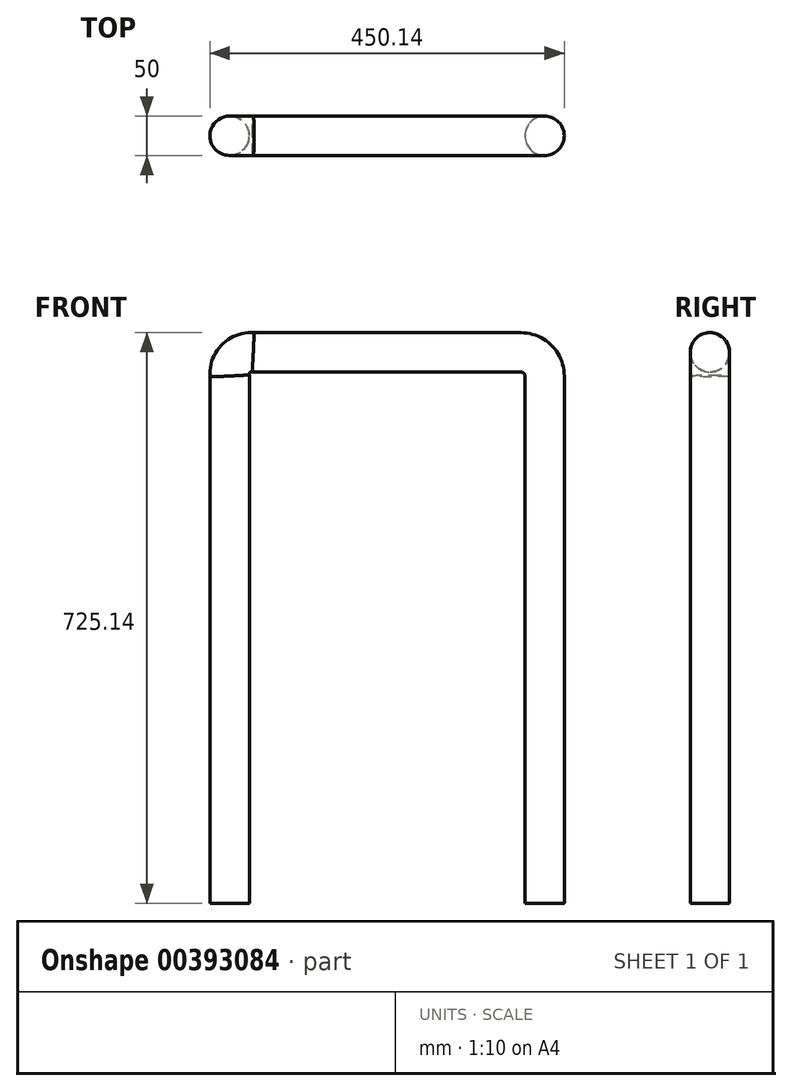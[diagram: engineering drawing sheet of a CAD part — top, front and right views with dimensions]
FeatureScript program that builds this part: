
annotation { "Feature Type Name" : "Feature", "Feature Type Description" : "" }
export const myFeature = defineFeature(function(context is Context, id is Id, definition is map)
    precondition{}
    {
        {
            var Q0;
            Q0=qCreatedBy(makeId("Top.planeOp"),FACE);
            var sketch = newSketch(context, id + "F0", { "sketchPlane" : qUnion([Q0])});
            skCircle(sketch, "E0", {"center": v(0, 0) * mm, "radius": 25 * mm});
            skSolve(sketch);
        }
        {
            var Q0;
            Q0=qCreatedBy(makeId("Front.planeOp"),FACE);
            var sketch = newSketch(context, id + "F1", { "sketchPlane" : qUnion([Q0])});
            skArc(sketch, "E1", {"start": v(400, 670) * mm, "mid": v(391.21, 691.21) * mm, "end": v(370, 700) * mm});
            skArc(sketch, "E2", {"start": v(30, 700) * mm, "mid": v(7.89, 692.11) * mm, "end": v(0, 670) * mm});
            skLineSegment(sketch, "E3", {"start": v(0, 670) * mm, "end": v(0, 0) * mm});
            skLineSegment(sketch, "E4", {"start": v(30, 700) * mm, "end": v(370, 700) * mm});
            skLineSegment(sketch, "E5", {"start": v(400, 670) * mm, "end": v(400, 0) * mm});
            skSolve(sketch);
        }
        {
            var Q0;
            Q0=makeQuery(id+"F0.imprint","IMPRINT",FACE,{"disambiguationData":[TD([[makeQuery(id+"F0.imprint","IMPRINT",EDGE,{"derivedFrom":sQuery(id+"F0.wireOp",EDGE,"E0")}),1.0]])]});
            var Q1;
            Q1=sQuery(id+"F1.wireOp",EDGE,"E3");
            var Q2;
            Q2=sQuery(id+"F1.wireOp",EDGE,"E2");
            var Q3;
            Q3=sQuery(id+"F1.wireOp",EDGE,"E1");
            var Q4;
            Q4=sQuery(id+"F1.wireOp",EDGE,"E5");
            var Q5;
            Q5=sQuery(id+"F1.wireOp",EDGE,"E4");
            sweep(context, id + "F2", {"profiles" : qUnion([Q0]), "path" : qUnion([Q1, Q2, Q3, Q4, Q5])});
        }
    });
